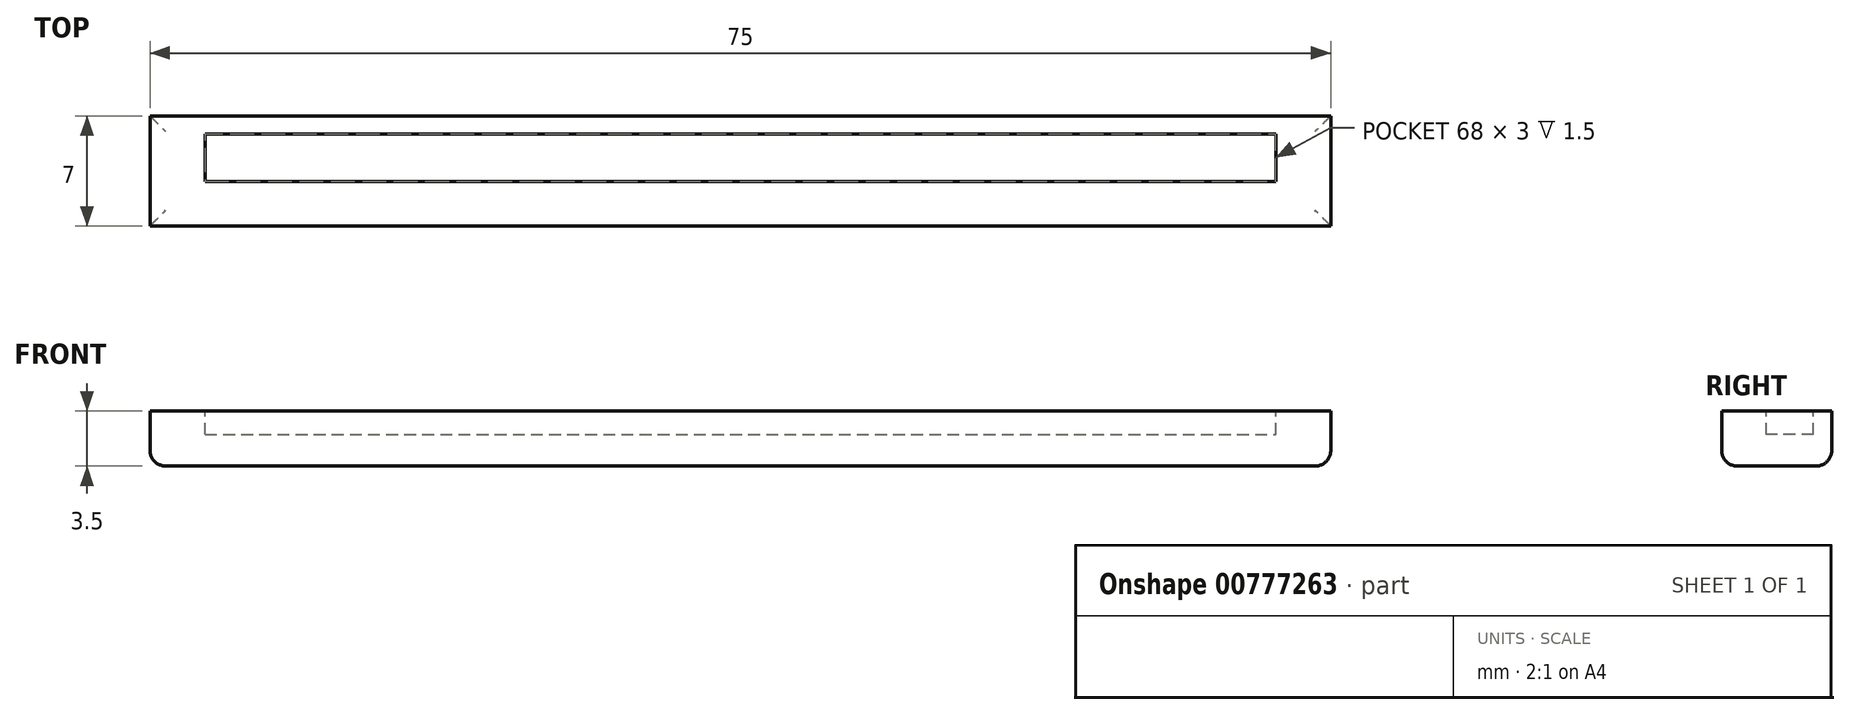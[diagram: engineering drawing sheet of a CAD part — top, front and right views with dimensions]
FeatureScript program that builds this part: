
annotation { "Feature Type Name" : "Feature", "Feature Type Description" : "" }
export const myFeature = defineFeature(function(context is Context, id is Id, definition is map)
    precondition{}
    {
        {
            var Q0;
            Q0=qCreatedBy(makeId("Top.planeOp"),FACE);
            var sketch = newSketch(context, id + "F0", { "sketchPlane" : qUnion([Q0])});
            skLineSegment(sketch, "E0.bottom", {"start": v(37.5, -3.5) * mm, "end": v(-37.5, -3.5) * mm});
            skLineSegment(sketch, "E0.top", {"start": v(37.5, 3.5) * mm, "end": v(-37.5, 3.5) * mm});
            skLineSegment(sketch, "E0.left", {"start": v(37.5, -3.5) * mm, "end": v(37.5, 3.5) * mm});
            skLineSegment(sketch, "E0.right", {"start": v(-37.5, -3.5) * mm, "end": v(-37.5, 3.5) * mm});
            skPoint(sketch, "E0.middle", {"position": v(0, 0) * mm});
            skSolve(sketch);
        }
        {
            var Q0;
            Q0=makeQuery(id+"F0.imprint","IMPRINT",FACE,{"disambiguationData":[TD([[makeQuery(id+"F0.imprint","IMPRINT",EDGE,{"derivedFrom":sQuery(id+"F0.wireOp",EDGE,"E0.bottom")}),-1.0]])]});
            extrude(context, id + "F1", {"entities" : qUnion([Q0]), "depth" : 3.5 * mm, "offsetDistance" : 25 * mm});
        }
        {
            var Q0;
            Q0=makeQuery(id+"F1.opExtrude","CAP_FACE",FACE,{"disambiguationData":[OSD([sQuery(id+"F0.wireOp",EDGE,"E0.bottom"),sQuery(id+"F0.wireOp",EDGE,"E0.top"),sQuery(id+"F0.wireOp",EDGE,"E0.left"),sQuery(id+"F0.wireOp",EDGE,"E0.right")])],"isStart":false});
            var sketch = newSketch(context, id + "F2", { "sketchPlane" : qUnion([Q0])});
            skLineSegment(sketch, "E1.bottom", {"start": v(-34, 2.33) * mm, "end": v(34, 2.33) * mm});
            skLineSegment(sketch, "E1.top", {"start": v(-34, -0.67) * mm, "end": v(34, -0.67) * mm});
            skLineSegment(sketch, "E1.left", {"start": v(-34, 2.33) * mm, "end": v(-34, -0.67) * mm});
            skLineSegment(sketch, "E1.right", {"start": v(34, 2.33) * mm, "end": v(34, -0.67) * mm});
            skSolve(sketch);
        }
        {
            var Q0;
            Q0=makeQuery(id+"F2.imprint","IMPRINT",FACE,{"disambiguationData":[TD([[makeQuery(id+"F2.imprint","IMPRINT",EDGE,{"derivedFrom":sQuery(id+"F2.wireOp",EDGE,"E1.bottom")}),-1.0]])]});
            extrude(context, id + "F3", {"entities" : qUnion([Q0]), "operationType" : NewBodyOperationType.REMOVE, "oppositeDirection" : true, "depth" : 1.5 * mm, "offsetDistance" : 25 * mm});
        }
        {
            var Q0;
            Q0=makeQuery(id+"F1.opExtrude","CAP_FACE",FACE,{"disambiguationData":[OSD([sQuery(id+"F0.wireOp",EDGE,"E0.bottom"),sQuery(id+"F0.wireOp",EDGE,"E0.top"),sQuery(id+"F0.wireOp",EDGE,"E0.left"),sQuery(id+"F0.wireOp",EDGE,"E0.right")])],"isStart":true});
            fillet(context, id + "F4", {"entities" : qUnion([Q0]), "radius" : 1 * mm, "tangentPropagation" : true, "allowEdgeOverflow" : false});
        }
    });
